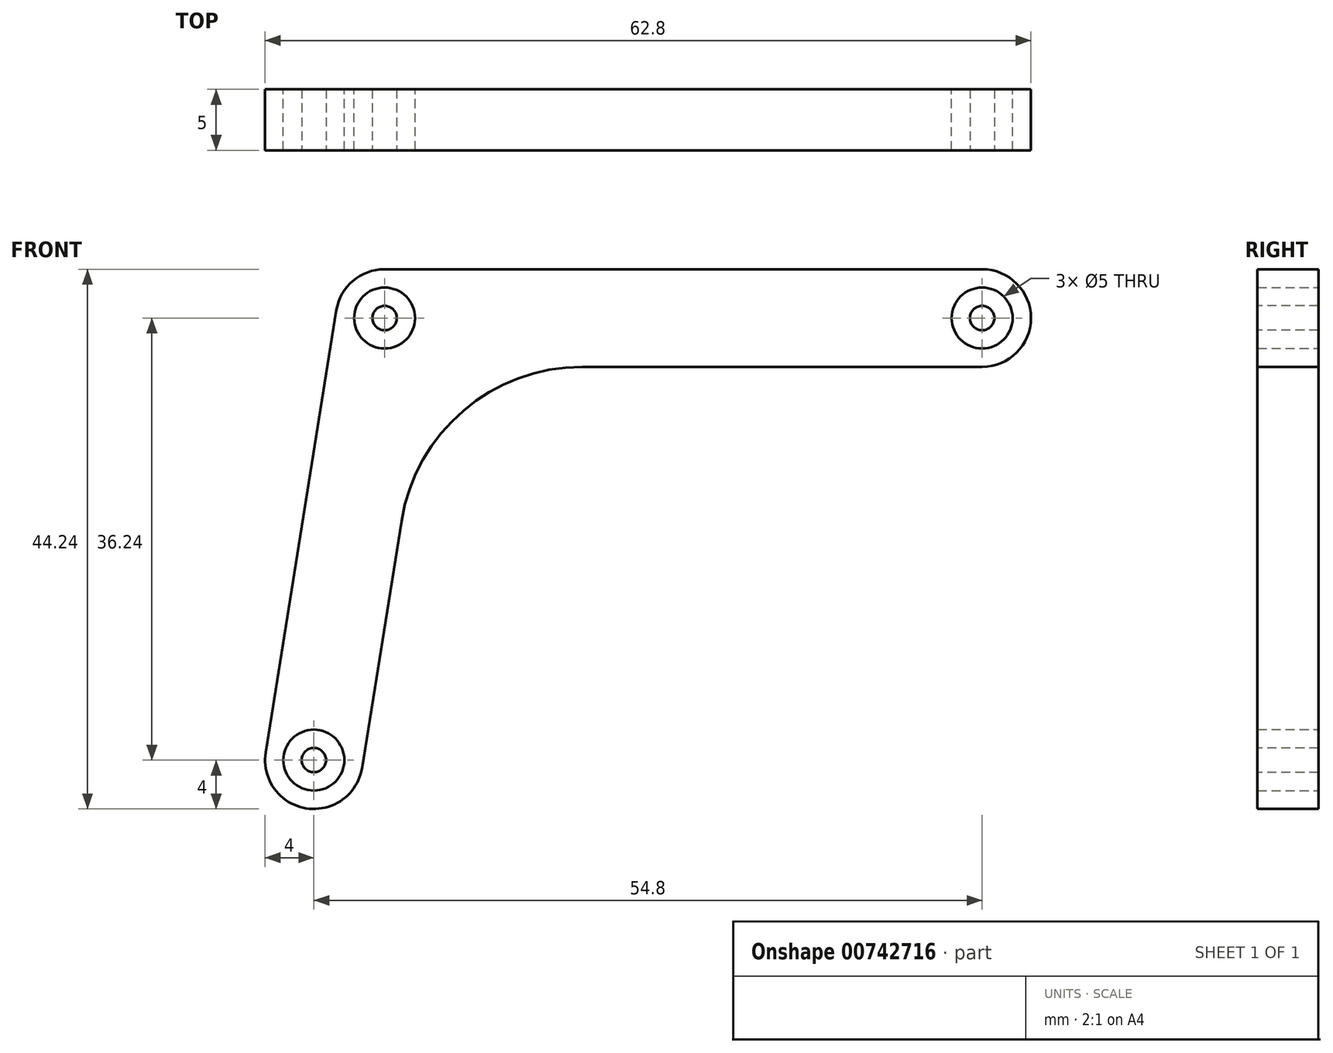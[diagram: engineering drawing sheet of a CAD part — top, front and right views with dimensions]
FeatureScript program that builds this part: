
annotation { "Feature Type Name" : "Feature", "Feature Type Description" : "" }
export const myFeature = defineFeature(function(context is Context, id is Id, definition is map)
    precondition{}
    {
        {
            var Q0;
            Q0=qCreatedBy(makeId("Front.planeOp"),FACE);
            var sketch = newSketch(context, id + "F0", { "sketchPlane" : qUnion([Q0])});
            skArc(sketch, "E0", {"start": v(0, 4) * mm, "mid": v(-2.6, 3.04) * mm, "end": v(-3.95, 0.63) * mm});
            skArc(sketch, "E1", {"start": v(-9.75, -35.6) * mm, "mid": v(-6.43, -40.19) * mm, "end": v(-1.85, -36.87) * mm});
            skArc(sketch, "E2", {"start": v(49, -4) * mm, "mid": v(53, 0) * mm, "end": v(49, 4) * mm});
            skLineSegment(sketch, "E3", {"start": v(0, 4) * mm, "end": v(49, 4) * mm});
            skLineSegment(sketch, "E4", {"start": v(-3.95, 0.63) * mm, "end": v(-9.75, -35.6) * mm});
            skLineSegment(sketch, "E5", {"start": v(-1.85, -36.87) * mm, "end": v(1.39, -16.63) * mm});
            skLineSegment(sketch, "E6", {"start": v(16.2, -4) * mm, "end": v(49, -4) * mm});
            skArc(sketch, "E7", {"start": v(16.2, -4) * mm, "mid": v(6.47, -7.59) * mm, "end": v(1.39, -16.63) * mm});
            skPoint(sketch, "E8.orphan", {"position": v(0, -4) * mm});
            skCircle(sketch, "E9", {"center": v(0, 0) * mm, "radius": 2.5 * mm});
            skCircle(sketch, "E10", {"center": v(-5.8, -36.24) * mm, "radius": 2.5 * mm});
            skCircle(sketch, "E11", {"center": v(49, 0) * mm, "radius": 2.5 * mm});
            skSolve(sketch);
        }
        {
            var Q0;
            Q0=makeQuery(id+"F0.imprint","IMPRINT",FACE,{"disambiguationData":[TD([[makeQuery(id+"F0.imprint","IMPRINT",EDGE,{"derivedFrom":sQuery(id+"F0.wireOp",EDGE,"E0")}),1.0]])]});
            extrude(context, id + "F1", {"entities" : qUnion([Q0]), "depth" : 5 * mm, "offsetDistance" : 25 * mm});
        }
        {
            var Q0;
            Q0=makeQuery(id+"F1.opExtrude","CAP_FACE",FACE,{"disambiguationData":[OSD([sQuery(id+"F0.wireOp",EDGE,"E0"),sQuery(id+"F0.wireOp",EDGE,"E1"),sQuery(id+"F0.wireOp",EDGE,"E2"),sQuery(id+"F0.wireOp",EDGE,"E3"),sQuery(id+"F0.wireOp",EDGE,"E4"),sQuery(id+"F0.wireOp",EDGE,"E5"),sQuery(id+"F0.wireOp",EDGE,"E6"),sQuery(id+"F0.wireOp",EDGE,"E7"),sQuery(id+"F0.wireOp",EDGE,"E9"),sQuery(id+"F0.wireOp",EDGE,"E10"),sQuery(id+"F0.wireOp",EDGE,"E11")])],"isStart":false});
            var sketch = newSketch(context, id + "F2", { "sketchPlane" : qUnion([Q0])});
            skCircle(sketch, "E12", {"center": v(0, 0) * mm, "radius": 2.5 * mm, "construction": true});
            skCircle(sketch, "E13", {"center": v(49, 0) * mm, "radius": 2.5 * mm, "construction": true});
            skCircle(sketch, "E14", {"center": v(-5.8, -36.24) * mm, "radius": 2.5 * mm, "construction": true});
            skCircle(sketch, "E15", {"center": v(-5.8, -36.24) * mm, "radius": 1 * mm});
            skCircle(sketch, "E16", {"center": v(0, 0) * mm, "radius": 1 * mm});
            skCircle(sketch, "E17", {"center": v(49, 0) * mm, "radius": 1 * mm});
            skSolve(sketch);
        }
        {
            var Q0;
            Q0 = qSketchRegion(id + "F2", true);
            extrude(context, id + "F3", {"entities" : qUnion([Q0]), "oppositeDirection" : true, "depth" : 5 * mm, "offsetDistance" : 25 * mm});
        }
    });
